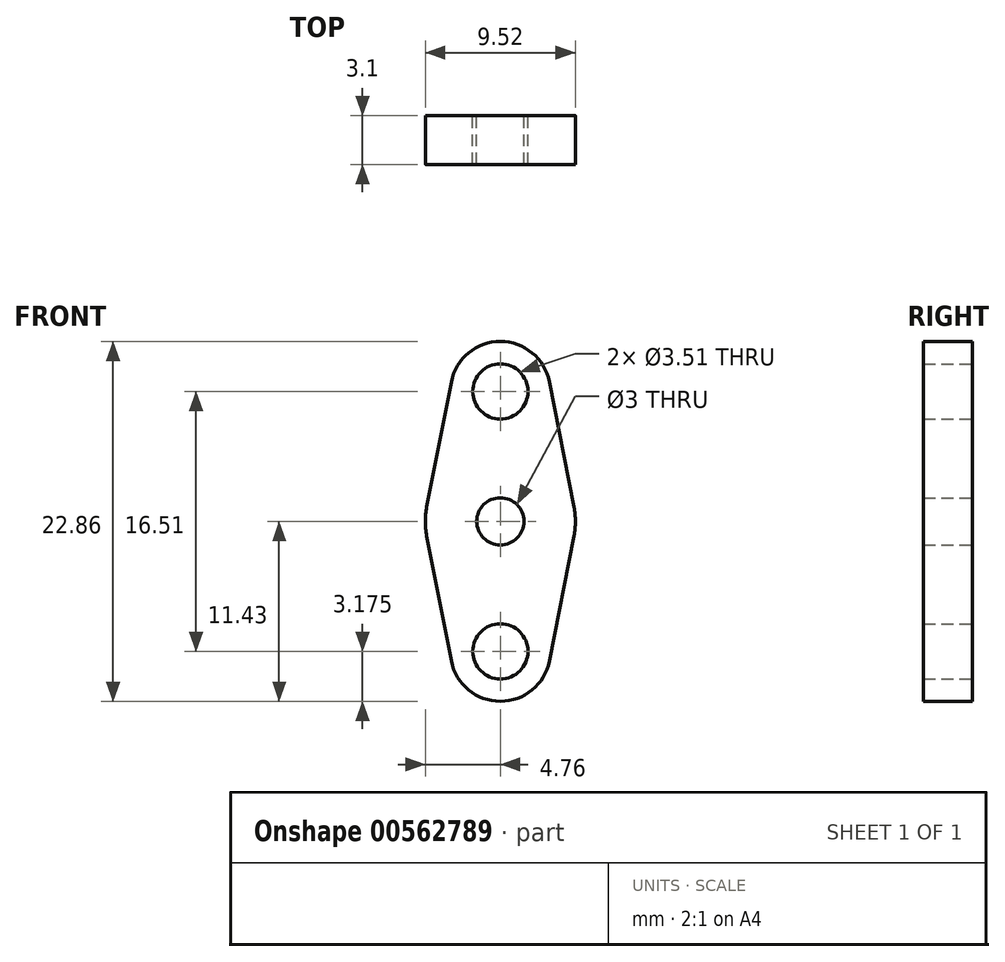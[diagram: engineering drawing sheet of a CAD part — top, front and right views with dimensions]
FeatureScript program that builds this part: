
annotation { "Feature Type Name" : "Feature", "Feature Type Description" : "" }
export const myFeature = defineFeature(function(context is Context, id is Id, definition is map)
    precondition{}
    {
        {
            var Q0;
            Q0=qCreatedBy(makeId("Front.planeOp"),FACE);
            var sketch = newSketch(context, id + "F0", { "sketchPlane" : qUnion([Q0])});
            skCircle(sketch, "E0", {"center": v(0, 0) * mm, "radius": 1.5 * mm});
            skCircle(sketch, "E1", {"center": v(0, 8.26) * mm, "radius": 1.75 * mm});
            skArc(sketch, "E2", {"start": v(3.12, 8.87) * mm, "mid": v(0, 11.43) * mm, "end": v(-3.12, 8.87) * mm});
            skLineSegment(sketch, "E3", {"start": v(-3.18, 8.26) * mm, "end": v(3.18, 8.26) * mm, "construction": true});
            skArc(sketch, "E4.MirrorCS", {"start": v(3.12, -8.87) * mm, "mid": v(0, -11.43) * mm, "end": v(-3.12, -8.87) * mm});
            skCircle(sketch, "E5.MirrorC", {"center": v(0, -8.26) * mm, "radius": 1.75 * mm});
            skPoint(sketch, "E6.end.orphan", {"position": v(-3.18, 0) * mm});
            skPoint(sketch, "E7.end.orphan", {"position": v(3.18, 0) * mm});
            skPoint(sketch, "E8.MirrorCS.start.orphan", {"position": v(3.18, -8.26) * mm});
            skPoint(sketch, "E9.MirrorCS.start.orphan", {"position": v(-3.17, -8.26) * mm});
            skArc(sketch, "E10", {"start": v(-4.67, 0.92) * mm, "mid": v(-4.76, 0) * mm, "end": v(-4.67, -0.92) * mm});
            skLineSegment(sketch, "E11", {"start": v(-3.12, 8.87) * mm, "end": v(-4.67, 0.92) * mm});
            skLineSegment(sketch, "E12.MirrorCS", {"start": v(3.12, 8.87) * mm, "end": v(4.67, 0.92) * mm});
            skLineSegment(sketch, "E13.MirrorCS", {"start": v(3.12, -8.87) * mm, "end": v(4.67, -0.92) * mm});
            skLineSegment(sketch, "E14.MirrorCS", {"start": v(-3.12, -8.87) * mm, "end": v(-4.67, -0.92) * mm});
            skArc(sketch, "E15.trimOffspring", {"start": v(4.67, -0.92) * mm, "mid": v(4.76, 0) * mm, "end": v(4.67, 0.92) * mm});
            skSolve(sketch);
        }
        {
            var Q0;
            Q0 = qSketchRegion(id + "F0", true);
            extrude(context, id + "F1", {"entities" : qUnion([Q0]), "depth" : 3.1 * mm, "offsetDistance" : 25.4 * mm});
        }
    });
